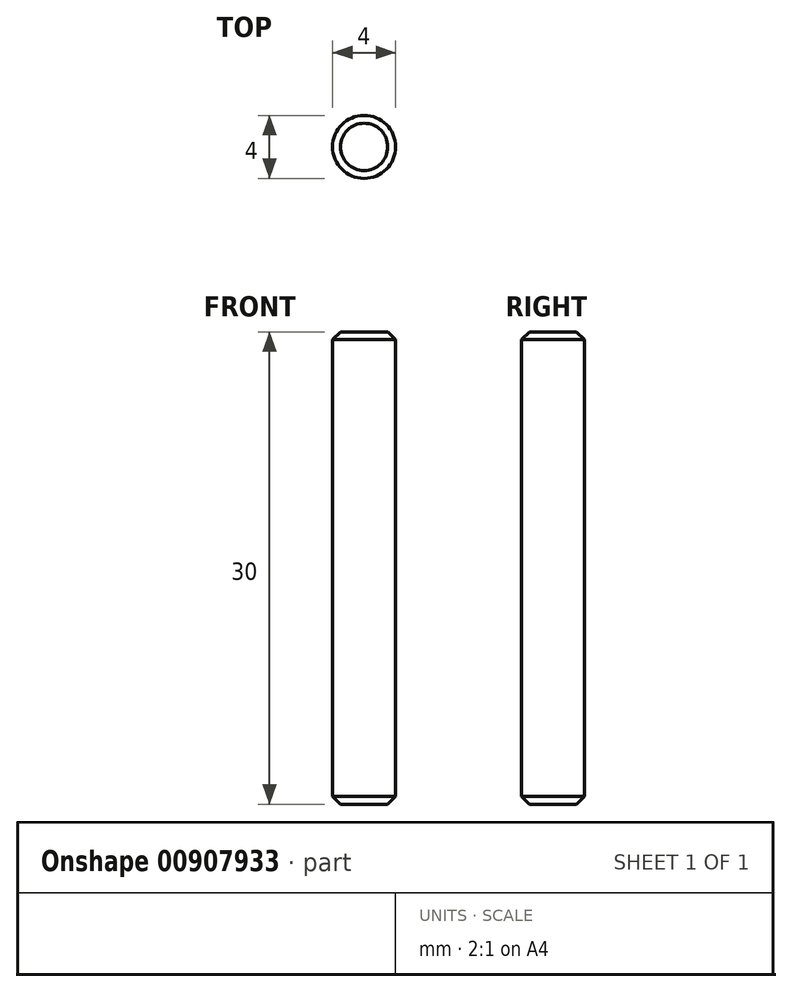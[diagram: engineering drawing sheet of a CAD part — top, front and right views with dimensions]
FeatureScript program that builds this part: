
annotation { "Feature Type Name" : "Feature", "Feature Type Description" : "" }
export const myFeature = defineFeature(function(context is Context, id is Id, definition is map)
    precondition{}
    {
        {
            var Q0;
            Q0=qCreatedBy(makeId("Top.planeOp"),FACE);
            var sketch = newSketch(context, id + "F0", { "sketchPlane" : qUnion([Q0])});
            skCircle(sketch, "E0", {"center": v(0, 0) * mm, "radius": 2 * mm});
            skSolve(sketch);
        }
        {
            var Q0;
            Q0 = qSketchRegion(id + "F0", true);
            extrude(context, id + "F1", {"entities" : qUnion([Q0]), "endBound" : BoundingType.SYMMETRIC, "depth" : 30 * mm, "offsetDistance" : 25 * mm});
        }
        {
            var Q0;
            Q0=makeQuery(id+"F1.opExtrude","CAP_FACE",FACE,{"disambiguationData":[OSD([sQuery(id+"F0.wireOp",EDGE,"E0")])],"isStart":false});
            var Q1;
            Q1=makeQuery(id+"F1.opExtrude","CAP_FACE",FACE,{"disambiguationData":[OSD([sQuery(id+"F0.wireOp",EDGE,"E0")])],"isStart":true});
            chamfer(context, id + "F2", {"entities" : qUnion([Q0, Q1]), "width" : 0.5 * mm, "tangentPropagation" : true});
        }
    });
